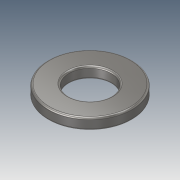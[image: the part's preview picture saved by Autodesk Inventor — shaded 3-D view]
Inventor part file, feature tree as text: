
AUTODESK INVENTOR PART (.ipt)
format: ipt  version: 2018.2 (Build 222227000, 227)  size: 118,272 bytes
history: native  units: mm
features: extrude x1, fillet x1, sketch x1
ambient origin geometry x8: Origin, YZ Plane, XZ Plane, XY Plane, X Axis, Y Axis, Z Axis, Center Point
bodies: Volumenkörper1 (feature_tree)
feature tree (3):
  extrude  "Extrusion1"  Depth=0.25mm
  fillet  "Rundung1"  Radius=1.6mm
  sketch  "Skizze1"  dims[d0=6.0mm d1=12.0mm d2=1.6mm d3=0.0mm d4=0.25mm]
